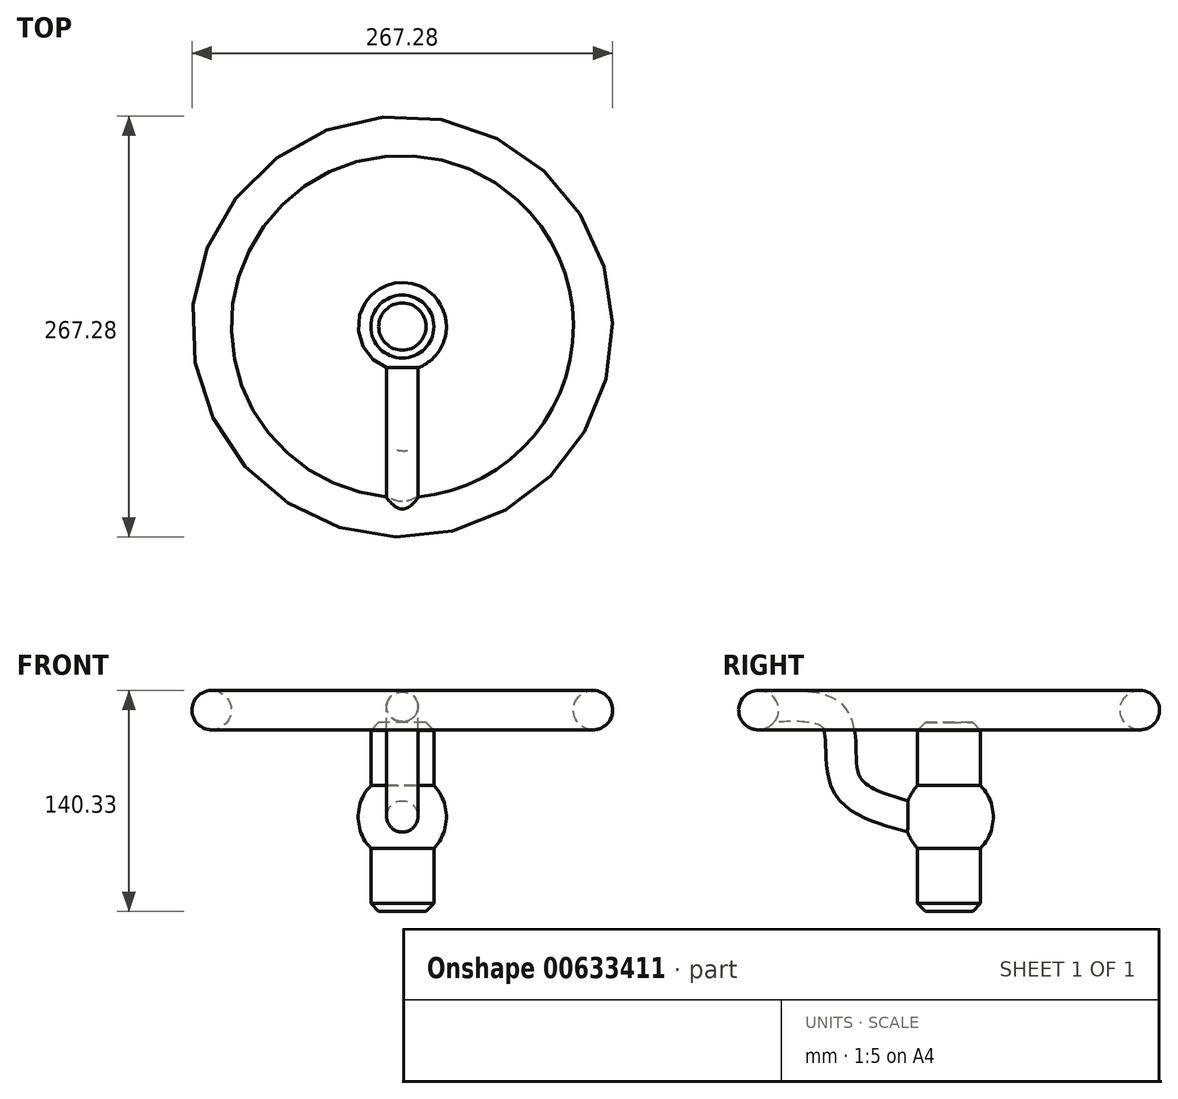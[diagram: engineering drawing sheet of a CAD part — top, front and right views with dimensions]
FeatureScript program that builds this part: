
annotation { "Feature Type Name" : "Feature", "Feature Type Description" : "" }
export const myFeature = defineFeature(function(context is Context, id is Id, definition is map)
    precondition{}
    {
        {
            var Q0;
            Q0=qCreatedBy(makeId("Front.planeOp"),FACE);
            var sketch = newSketch(context, id + "F0", { "sketchPlane" : qUnion([Q0])});
            skLineSegment(sketch, "E0", {"start": v(0, 60) * mm, "end": v(0, -60) * mm});
            skLineSegment(sketch, "E1", {"start": v(0, -60) * mm, "end": v(20, -60) * mm});
            skLineSegment(sketch, "E2", {"start": v(20, -60) * mm, "end": v(20, -20) * mm});
            skLineSegment(sketch, "E3", {"start": v(0, 60) * mm, "end": v(20, 60) * mm});
            skLineSegment(sketch, "E4", {"start": v(20, 60) * mm, "end": v(20, 20) * mm});
            skArc(sketch, "E5", {"start": v(20, -20) * mm, "mid": v(28, 0) * mm, "end": v(20, 20) * mm});
            skSolve(sketch);
        }
        {
            var Q0;
            Q0=makeQuery(id+"F0.imprint","IMPRINT",FACE,{"disambiguationData":[TD([[makeQuery(id+"F0.imprint","IMPRINT",EDGE,{"derivedFrom":sQuery(id+"F0.wireOp",EDGE,"E0")}),1.0]])]});
            var Q1;
            Q1=sQuery(id+"F0.wireOp",EDGE,"E0");
            revolve(context, id + "F1", {"entities" : qUnion([Q0]), "axis" : qUnion([Q1]), "revolveType" : RevolveType.FULL});
        }
        {
            var Q0;
            Q0=makeQuery(id+"F1.opRevolve","SWEPT_EDGE",EDGE,{"disambiguationData":[OSD([sQuery(id+"F0.wireOp",EDGE,"E3"),sQuery(id+"F0.wireOp",EDGE,"E4")])]});
            var Q1;
            Q1=makeQuery(id+"F1.opRevolve","SWEPT_EDGE",EDGE,{"disambiguationData":[OSD([sQuery(id+"F0.wireOp",EDGE,"E1"),sQuery(id+"F0.wireOp",EDGE,"E2")])]});
            chamfer(context, id + "F2", {"entities" : qUnion([Q0, Q1]), "width" : 5 * mm, "tangentPropagation" : true});
        }
        {
            var Q0;
            Q0=qCreatedBy(makeId("Front.planeOp"),FACE);
            cPlane(context, id + "F3", {"entities" : qUnion([Q0]), "cplaneType" : CPlaneType.OFFSET, "offset" : 25 * mm, "width" : 150 * mm, "height" : 150 * mm});
        }
        {
            var Q0;
            Q0=qCreatedBy(id+"F3.planeOp",FACE);
            var sketch = newSketch(context, id + "F4", { "sketchPlane" : qUnion([Q0])});
            skCircle(sketch, "E6", {"center": v(0, 0) * mm, "radius": 10 * mm});
            skSolve(sketch);
        }
        {
            var Q0;
            Q0=qCreatedBy(makeId("Right.planeOp"),FACE);
            var sketch = newSketch(context, id + "F5", { "sketchPlane" : qUnion([Q0])});
            skFitSpline(sketch, "E7", {"points": [v(-25, 0) * mm, v(-65.57, 22.18) * mm, v(-72.59, 61.96) * mm, v(-116.45, 69.58) * mm], "startDerivative": vector(-152.03, 41.55) * mm, "endDerivative": vector(-166.2, -8.86) * mm});
            skSolve(sketch);
        }
        {
            var Q0;
            Q0 = qSketchRegion(id + "F4", true);
            var Q1;
            Q1=sQuery(id+"F5.wireOp",EDGE,"E7");
            sweep(context, id + "F6", {"operationType" : NewBodyOperationType.ADD, "profiles" : qUnion([Q0]), "path" : qUnion([Q1])});
        }
        {
            var Q0;
            Q0=qCreatedBy(makeId("Right.planeOp"),FACE);
            var sketch = newSketch(context, id + "F7", { "sketchPlane" : qUnion([Q0])});
            skCircle(sketch, "E8", {"center": v(-121.14, 67.83) * mm, "radius": 12.5 * mm});
            skSolve(sketch);
        }
        {
            var Q0;
            Q0 = qSketchRegion(id + "F7", true);
            var Q1;
            Q1=makeQuery(id+"F1.opRevolve","SWEPT_FACE",FACE,{"disambiguationData":[OSD([sQuery(id+"F0.wireOp",EDGE,"E4")])]});
            revolve(context, id + "F8", {"operationType" : NewBodyOperationType.ADD, "entities" : qUnion([Q0]), "axis" : qUnion([Q1]), "revolveType" : RevolveType.FULL});
        }
        {
            var Q0;
            Q0 = qSketchRegion(id + "F7", true);
            var Q1;
            Q1=makeQuery(id+"F1.opRevolve","SWEPT_FACE",FACE,{"disambiguationData":[OSD([sQuery(id+"F0.wireOp",EDGE,"E5")])]});
            revolve(context, id + "F9", {"operationType" : NewBodyOperationType.ADD, "entities" : qUnion([Q0]), "axis" : qUnion([Q1]), "revolveType" : RevolveType.FULL});
        }
    });
